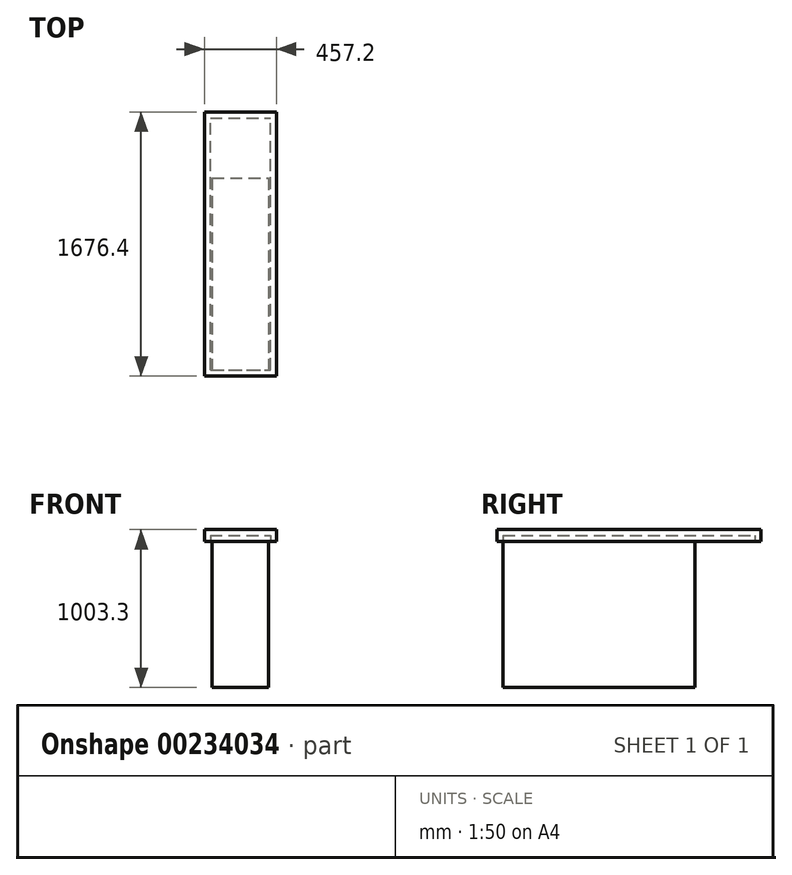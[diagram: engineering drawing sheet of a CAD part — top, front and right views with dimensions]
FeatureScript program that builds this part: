
annotation { "Feature Type Name" : "Feature", "Feature Type Description" : "" }
export const myFeature = defineFeature(function(context is Context, id is Id, definition is map)
    precondition{}
    {
        {
            var Q0;
            Q0=qCreatedBy(makeId("Front.planeOp"),FACE);
            var sketch = newSketch(context, id + "F0", { "sketchPlane" : qUnion([Q0])});
            skLineSegment(sketch, "E0.bottom", {"start": v(-228.6, 38.1) * mm, "end": v(228.6, 38.1) * mm});
            skLineSegment(sketch, "E0.top", {"start": v(-228.6, -38.1) * mm, "end": v(228.6, -38.1) * mm});
            skLineSegment(sketch, "E0.left", {"start": v(-228.6, 38.1) * mm, "end": v(-228.6, -38.1) * mm});
            skLineSegment(sketch, "E0.right", {"start": v(228.6, 38.1) * mm, "end": v(228.6, -38.1) * mm});
            skSolve(sketch);
        }
        {
            var Q0;
            Q0 = qSketchRegion(id + "F0", true);
            extrude(context, id + "F1", {"entities" : qUnion([Q0]), "depth" : 1676.4 * mm});
        }
        {
            var Q0;
            Q0=makeQuery(id+"F1.opExtrude","SWEPT_FACE",FACE,{"disambiguationData":[OSD([sQuery(id+"F0.wireOp",EDGE,"E0.top")])]});
            var sketch = newSketch(context, id + "F2", { "sketchPlane" : qUnion([Q0])});
            skLineSegment(sketch, "E1.bottom", {"start": v(-190.5, 1638.3) * mm, "end": v(190.5, 1638.3) * mm});
            skLineSegment(sketch, "E1.top", {"start": v(-190.5, 38.1) * mm, "end": v(190.5, 38.1) * mm});
            skLineSegment(sketch, "E1.left", {"start": v(-190.5, 1638.3) * mm, "end": v(-190.5, 38.1) * mm});
            skLineSegment(sketch, "E1.right", {"start": v(190.5, 1638.3) * mm, "end": v(190.5, 38.1) * mm});
            skSolve(sketch);
        }
        {
            var Q0;
            Q0=makeQuery(id+"F1.opExtrude","SWEPT_FACE",FACE,{"disambiguationData":[OSD([sQuery(id+"F0.wireOp",EDGE,"E0.top")])]});
            shell(context, id + "F3", {"entities" : qUnion([Q0]), "thickness" : 38.1 * mm});
        }
        {
            var Q0;
            Q0=makeQuery(id+"F2.imprint","IMPRINT",FACE,{"disambiguationData":[TD([[makeQuery(id+"F2.imprint","IMPRINT",EDGE,{"derivedFrom":sQuery(id+"F2.wireOp",EDGE,"E1.bottom")}),-1.0]])]});
            var sketch = newSketch(context, id + "F4", { "sketchPlane" : qUnion([Q0])});
            skLineSegment(sketch, "E2.bottom", {"start": v(-177.8, 419.1) * mm, "end": v(177.8, 419.1) * mm});
            skLineSegment(sketch, "E2.top", {"start": v(-177.8, 1638.3) * mm, "end": v(177.8, 1638.3) * mm});
            skLineSegment(sketch, "E2.left", {"start": v(-177.8, 419.1) * mm, "end": v(-177.8, 1638.3) * mm});
            skLineSegment(sketch, "E2.right", {"start": v(177.8, 419.1) * mm, "end": v(177.8, 1638.3) * mm});
            skSolve(sketch);
        }
        {
            var Q0;
            Q0 = qSketchRegion(id + "F4", true);
            extrude(context, id + "F5", {"entities" : qUnion([Q0]), "depth" : 927.1 * mm});
        }
    });
